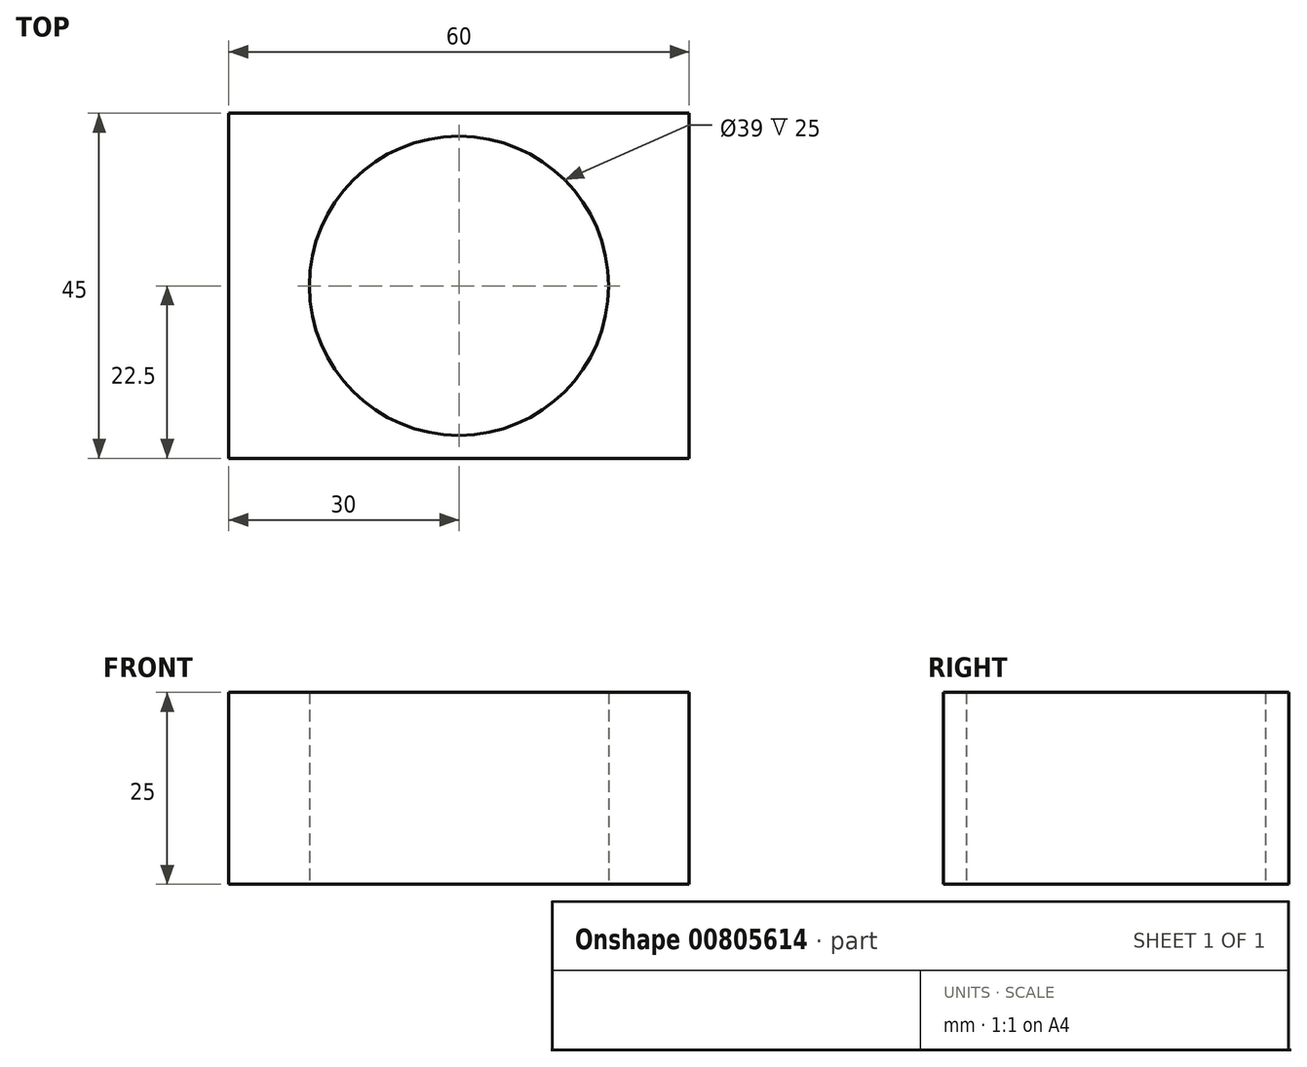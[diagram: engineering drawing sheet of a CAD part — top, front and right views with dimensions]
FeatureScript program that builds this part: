
annotation { "Feature Type Name" : "Feature", "Feature Type Description" : "" }
export const myFeature = defineFeature(function(context is Context, id is Id, definition is map)
    precondition{}
    {
        {
            var Q0;
            Q0=qCreatedBy(makeId("Top.planeOp"),FACE);
            var sketch = newSketch(context, id + "F0", { "sketchPlane" : qUnion([Q0])});
            skCircle(sketch, "E0", {"center": v(0, 0) * mm, "radius": 22.5 * mm});
            skSolve(sketch);
        }
        {
            var Q0;
            Q0=qSketchRegion(id+"F0",true);
            extrude(context, id + "F1", {"entities" : qUnion([Q0]), "depth" : 25 * mm, "offsetDistance" : 25 * mm});
        }
        {
            var Q0;
            Q0=qCreatedBy(makeId("Top.planeOp"),FACE);
            var sketch = newSketch(context, id + "F2", { "sketchPlane" : qUnion([Q0])});
            skCircle(sketch, "E1", {"center": v(0, 0) * mm, "radius": 19.5 * mm});
            skSolve(sketch);
        }
        {
            var Q0;
            Q0=qSketchRegion(id+"F2",true);
            extrude(context, id + "F3", {"entities" : qUnion([Q0]), "operationType" : NewBodyOperationType.REMOVE, "endBound" : BoundingType.THROUGH_ALL, "depth" : 20 * mm, "offsetDistance" : 25 * mm});
        }
        {
            var Q0;
            Q0=makeQuery(id+"F1.opExtrude","CAP_FACE",FACE,{"disambiguationData":[OSD([sQuery(id+"F0.wireOp",EDGE,"E0")])],"isStart":true});
            var sketch = newSketch(context, id + "F4", { "sketchPlane" : qUnion([Q0])});
            skLineSegment(sketch, "E2.bottom", {"start": v(30, -22.5) * mm, "end": v(-30, -22.5) * mm});
            skLineSegment(sketch, "E2.top", {"start": v(30, 22.5) * mm, "end": v(-30, 22.5) * mm});
            skLineSegment(sketch, "E2.left", {"start": v(30, -22.5) * mm, "end": v(30, 22.5) * mm});
            skLineSegment(sketch, "E2.right", {"start": v(-30, -22.5) * mm, "end": v(-30, 22.5) * mm});
            skPoint(sketch, "E2.middle", {"position": v(0, 0) * mm});
            skSolve(sketch);
        }
        {
            var Q0;
            {var subQ0=sQuery(id+"F4.wireOp",EDGE,"E2.right");var subQ1=sQuery(id+"F4.wireOp",EDGE,"E2.top");var subQ2=makeQuery(id+"F4.imprint","INTERSECT",VERTEX,{"derivedFrom":[subQ1,subQ0]});Q0=makeQuery(id+"F4.imprint","IMPRINT",FACE,{"disambiguationData":[TD([[makeQuery(id+"F4.imprint","IMPRINT",EDGE,{"disambiguationData":[TD([[subQ2,1.0]])],"derivedFrom":subQ1}),1.0]])]});}
            var Q1;
            {var subQ0=sQuery(id+"F4.wireOp",EDGE,"E2.left");var subQ1=sQuery(id+"F4.wireOp",EDGE,"E2.top");var subQ2=makeQuery(id+"F4.imprint","INTERSECT",VERTEX,{"derivedFrom":[subQ1,subQ0]});Q1=makeQuery(id+"F4.imprint","IMPRINT",FACE,{"disambiguationData":[TD([[makeQuery(id+"F4.imprint","IMPRINT",EDGE,{"disambiguationData":[TD([[subQ2,-1.0]])],"derivedFrom":subQ1}),1.0]])]});}
            extrude(context, id + "F5", {"entities" : qUnion([Q0, Q1]), "operationType" : NewBodyOperationType.ADD, "oppositeDirection" : true, "depth" : 25 * mm, "offsetDistance" : 25 * mm});
        }
    });
